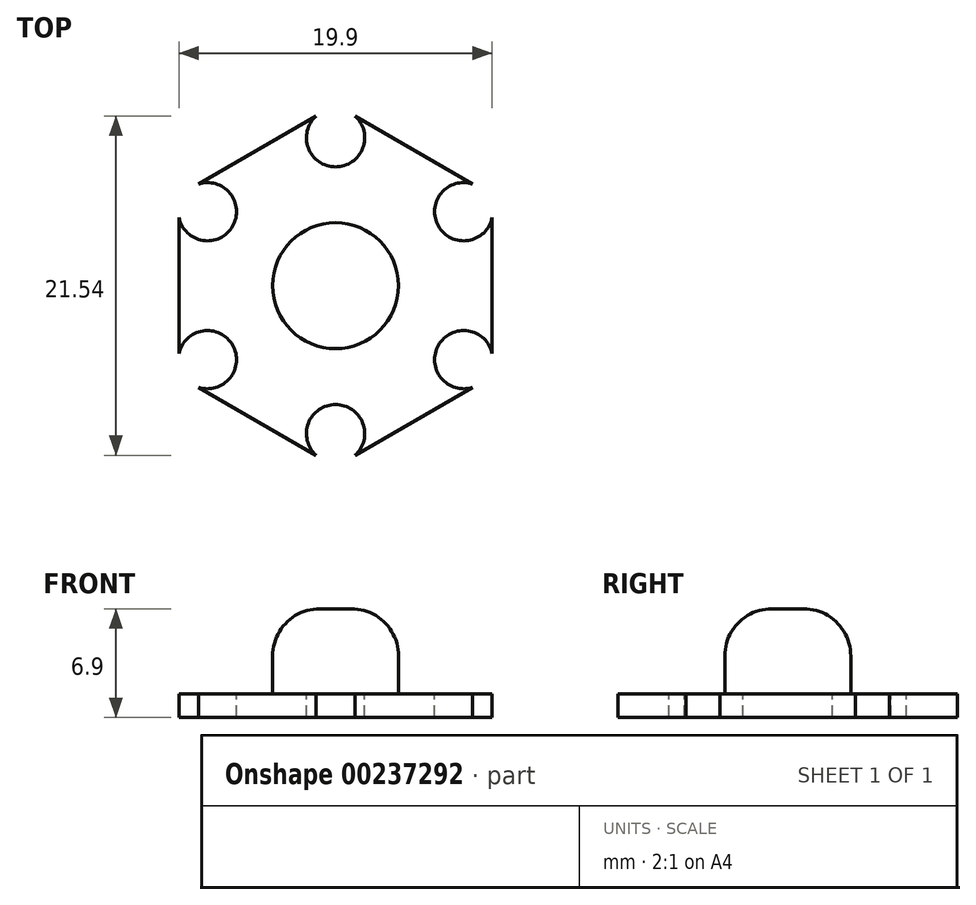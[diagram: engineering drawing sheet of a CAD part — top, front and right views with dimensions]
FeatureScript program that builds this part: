
annotation { "Feature Type Name" : "Feature", "Feature Type Description" : "" }
export const myFeature = defineFeature(function(context is Context, id is Id, definition is map)
    precondition{}
    {
        {
            var Q0;
            Q0=qCreatedBy(makeId("Top.planeOp"),FACE);
            var sketch = newSketch(context, id + "F0", { "sketchPlane" : qUnion([Q0])});
            skCircle(sketch, "E0.cCircle", {"center": v(0, 0) * mm, "radius": 9.95 * mm, "construction": true});
            skLineSegment(sketch, "E0.0", {"start": v(9.95, 4.31) * mm, "end": v(9.95, -4.31) * mm});
            skLineSegment(sketch, "E0.1", {"start": v(8.71, -6.46) * mm, "end": v(1.24, -10.77) * mm});
            skLineSegment(sketch, "E0.3", {"start": v(-9.95, -4.31) * mm, "end": v(-9.95, 4.31) * mm});
            skLineSegment(sketch, "E0.4", {"start": v(-8.71, 6.46) * mm, "end": v(-1.24, 10.77) * mm});
            skLineSegment(sketch, "E0.5", {"start": v(1.24, 10.77) * mm, "end": v(8.71, 6.46) * mm});
            skPoint(sketch, "E0.0.midPoint", {"position": v(9.95, 0) * mm});
            skCircle(sketch, "E1", {"center": v(0, 0) * mm, "radius": 7.55 * mm, "construction": true});
            skLineSegment(sketch, "E2", {"start": v(0, 0) * mm, "end": v(9.95, -5.74) * mm, "construction": true});
            skArc(sketch, "E3", {"start": v(9.95, -4.31) * mm, "mid": v(6.54, -3.78) * mm, "end": v(8.71, -6.46) * mm});
            skArc(sketch, "E4.1.0", {"start": v(8.71, 6.46) * mm, "mid": v(6.54, 3.78) * mm, "end": v(9.95, 4.31) * mm});
            skArc(sketch, "E4.2.0", {"start": v(-1.24, 10.77) * mm, "mid": v(0, 7.55) * mm, "end": v(1.24, 10.77) * mm});
            skArc(sketch, "E4.3.0", {"start": v(-9.95, 4.31) * mm, "mid": v(-6.54, 3.77) * mm, "end": v(-8.71, 6.46) * mm});
            skArc(sketch, "E4.4.0", {"start": v(-8.71, -6.46) * mm, "mid": v(-6.54, -3.78) * mm, "end": v(-9.95, -4.31) * mm});
            skArc(sketch, "E4.5.0", {"start": v(1.24, -10.77) * mm, "mid": v(0, -7.55) * mm, "end": v(-1.24, -10.77) * mm});
            skPoint(sketch, "E5.orphan", {"position": v(-9.95, 5.74) * mm});
            skPoint(sketch, "E6.orphan", {"position": v(-9.95, -5.74) * mm});
            skLineSegment(sketch, "E7.trimOffspring", {"start": v(-1.24, -10.77) * mm, "end": v(-8.71, -6.46) * mm});
            skPoint(sketch, "E8.orphan", {"position": v(9.95, 5.74) * mm});
            skPoint(sketch, "E9.orphan", {"position": v(0, 11.49) * mm});
            skSolve(sketch);
        }
        {
            var Q0;
            Q0=makeQuery(id+"F0.imprint","IMPRINT",FACE,{"disambiguationData":[TD([[makeQuery(id+"F0.imprint","IMPRINT",EDGE,{"derivedFrom":sQuery(id+"F0.wireOp",EDGE,"E0.0")}),-1.0]])]});
            extrude(context, id + "F1", {"entities" : qUnion([Q0]), "oppositeDirection" : true, "depth" : 1.5 * mm});
        }
        {
            var Q0;
            Q0=makeQuery(id+"F1.opExtrude","CAP_FACE",FACE,{"disambiguationData":[OSD([sQuery(id+"F0.wireOp",EDGE,"E0.0"),sQuery(id+"F0.wireOp",EDGE,"E0.1"),sQuery(id+"F0.wireOp",EDGE,"E0.3"),sQuery(id+"F0.wireOp",EDGE,"E0.4"),sQuery(id+"F0.wireOp",EDGE,"E0.5"),sQuery(id+"F0.wireOp",EDGE,"E3"),sQuery(id+"F0.wireOp",EDGE,"E4.1.0"),sQuery(id+"F0.wireOp",EDGE,"E4.2.0"),sQuery(id+"F0.wireOp",EDGE,"E4.3.0"),sQuery(id+"F0.wireOp",EDGE,"E4.4.0"),sQuery(id+"F0.wireOp",EDGE,"E4.5.0"),sQuery(id+"F0.wireOp",EDGE,"E7.trimOffspring")])],"isStart":true});
            var sketch = newSketch(context, id + "F2", { "sketchPlane" : qUnion([Q0])});
            skCircle(sketch, "E10", {"center": v(0, 0) * mm, "radius": 4 * mm});
            skSolve(sketch);
        }
        {
            var Q0;
            Q0=makeQuery(id+"F2.imprint","IMPRINT",FACE,{"disambiguationData":[TD([[makeQuery(id+"F2.imprint","IMPRINT",EDGE,{"derivedFrom":sQuery(id+"F2.wireOp",EDGE,"E10")}),1.0]])]});
            extrude(context, id + "F3", {"entities" : qUnion([Q0]), "operationType" : NewBodyOperationType.ADD, "depth" : 5.4 * mm});
        }
        {
            var Q0;
            Q0=makeQuery(id+"F3.opExtrude","CAP_EDGE",EDGE,{"disambiguationData":[OSD([sQuery(id+"F2.wireOp",EDGE,"E10")])],"isStart":false});
            fillet(context, id + "F4", {"entities" : qUnion([Q0]), "radius" : 3 * mm, "tangentPropagation" : true, "allowEdgeOverflow" : false});
        }
    });
